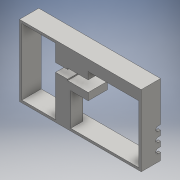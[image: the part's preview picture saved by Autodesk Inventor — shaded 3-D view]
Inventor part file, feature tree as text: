
AUTODESK INVENTOR PART (.ipt)
format: ipt  version: 2016 (Build 200138000, 138)  size: 174,080 bytes
history: native  units: mm
features: sketch x3, extrude x3, fillet x1
ambient origin geometry x8: Origin, YZ Plane, XZ Plane, XY Plane, X Axis, Y Axis, Z Axis, Center Point
bodies: Body1 (feature_tree)
feature tree (7):
  sketch  "Sketch1"  dims[d2=2.5mm d3=10.0mm]
  extrude  "Extrusion5"  Depth=10.0mm
  extrude  "Extrusion6"  Depth=21.0mm
  extrude  "Extrusion7"  Depth=28.0mm
  fillet  "Fillet1"  Radius=55.0mm
  sketch  "Sketch2"  dims[d4=7.0mm d5=21.0mm]
  sketch  "Sketch3"  dims[d6=42.0mm d9=28.0mm d10=55.0mm d13=10.0mm d14=9.0mm d15=17.0mm d16=2.0mm d17=2.0mm d20=2.0mm d24=10.0mm d25=0.0mm d26=16.0mm d27=0.0mm d28=101.0mm d29=59.0mm d30=4.0mm d31=4.0mm d32=0.0mm d33=2.0mm d34=42.0mm d35=27.0mm d36=56.5mm d37=12.5mm]
